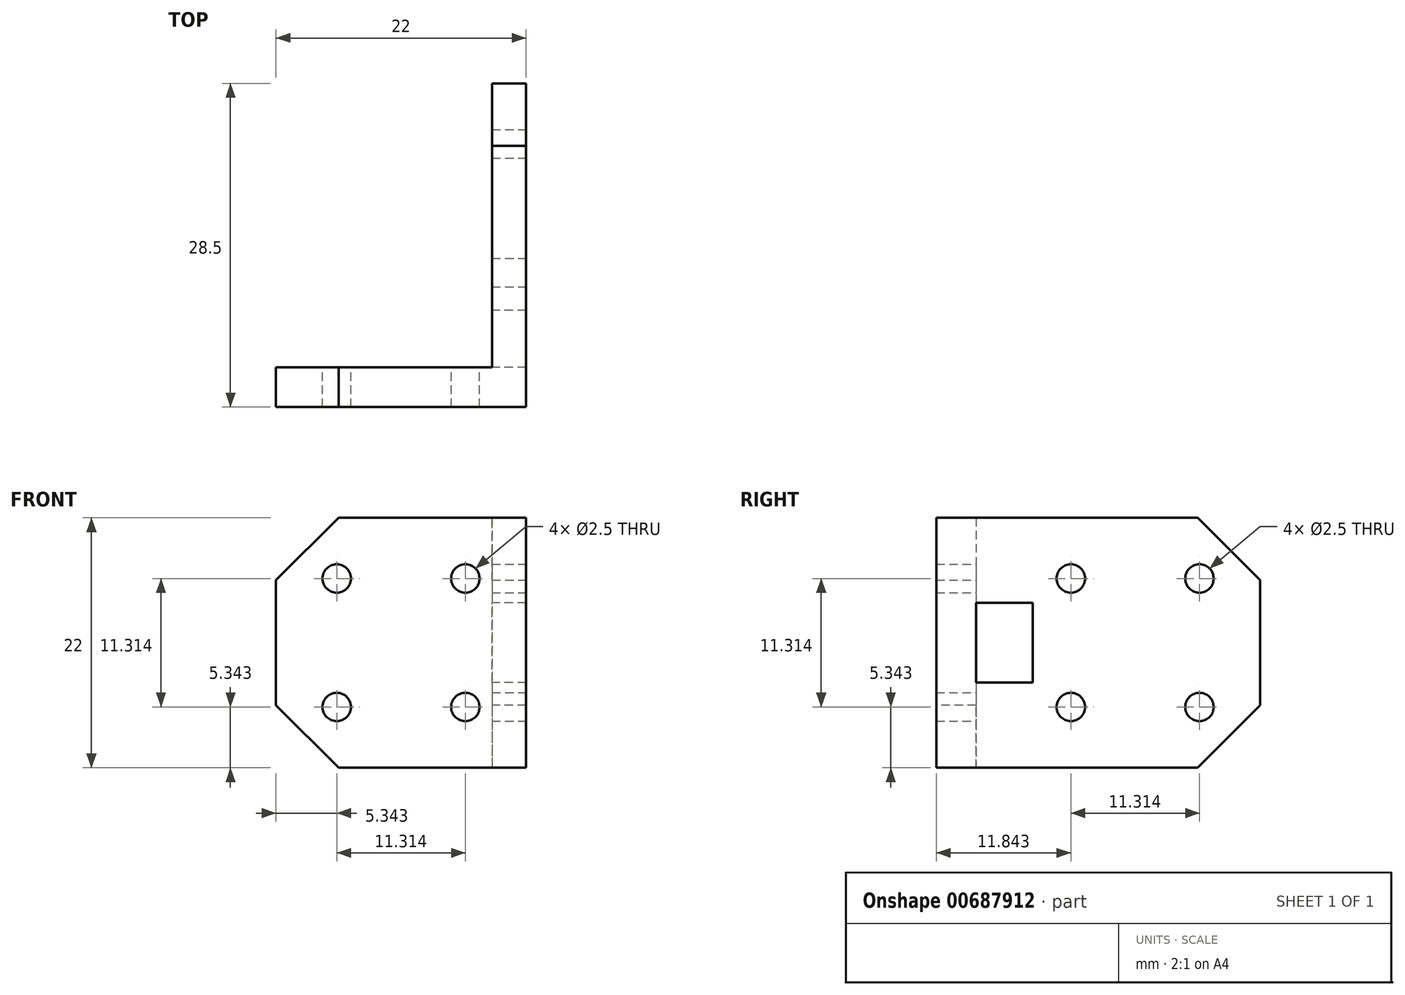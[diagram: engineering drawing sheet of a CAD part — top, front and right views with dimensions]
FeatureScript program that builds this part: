
annotation { "Feature Type Name" : "Feature", "Feature Type Description" : "" }
export const myFeature = defineFeature(function(context is Context, id is Id, definition is map)
    precondition{}
    {
        {
            var Q0;
            Q0=qCreatedBy(makeId("Top.planeOp"),FACE);
            var sketch = newSketch(context, id + "F0", { "sketchPlane" : qUnion([Q0])});
            skLineSegment(sketch, "E0", {"start": v(8, 11) * mm, "end": v(11, 11) * mm});
            skLineSegment(sketch, "E1", {"start": v(11, 11) * mm, "end": v(11, -17.5) * mm});
            skLineSegment(sketch, "E2", {"start": v(11, -17.5) * mm, "end": v(-11, -17.5) * mm});
            skLineSegment(sketch, "E3", {"start": v(-11, -17.5) * mm, "end": v(-11, -14) * mm});
            skLineSegment(sketch, "E4", {"start": v(-11, -14) * mm, "end": v(8, -14) * mm});
            skLineSegment(sketch, "E5", {"start": v(8, -14) * mm, "end": v(8, 11) * mm});
            skSolve(sketch);
        }
        {
            var Q0;
            Q0 = qSketchRegion(id + "F0", true);
            extrude(context, id + "F1", {"entities" : qUnion([Q0]), "endBound" : BoundingType.SYMMETRIC, "depth" : 22 * mm, "offsetDistance" : 25 * mm});
        }
        {
            var Q0;
            Q0=makeQuery(id+"F1.opExtrude","SWEPT_FACE",FACE,{"disambiguationData":[OSD([sQuery(id+"F0.wireOp",EDGE,"E1")])]});
            var sketch = newSketch(context, id + "F2", { "sketchPlane" : qUnion([Q0])});
            skCircle(sketch, "E6", {"center": v(5.66, -5.66) * mm, "radius": 1.25 * mm});
            skLineSegment(sketch, "E7", {"start": v(0, 0) * mm, "end": v(11, -11) * mm, "construction": true});
            skCircle(sketch, "E8.1.0", {"center": v(5.66, 5.66) * mm, "radius": 1.25 * mm});
            skCircle(sketch, "E8.2.0", {"center": v(-5.66, 5.66) * mm, "radius": 1.25 * mm});
            skCircle(sketch, "E8.3.0", {"center": v(-5.66, -5.66) * mm, "radius": 1.25 * mm});
            skPoint(sketch, "E8.center", {"position": v(0, 0) * mm});
            skSolve(sketch);
        }
        {
            var Q0;
            Q0 = qSketchRegion(id + "F2", true);
            extrude(context, id + "F3", {"entities" : qUnion([Q0]), "operationType" : NewBodyOperationType.REMOVE, "endBound" : BoundingType.THROUGH_ALL, "oppositeDirection" : true, "depth" : 25 * mm, "offsetDistance" : 25 * mm});
        }
        {
            var Q0;
            Q0=makeQuery(id+"F1.opExtrude","SWEPT_FACE",FACE,{"disambiguationData":[OSD([sQuery(id+"F0.wireOp",EDGE,"E4")])]});
            var sketch = newSketch(context, id + "F4", { "sketchPlane" : qUnion([Q0])});
            skCircle(sketch, "E9", {"center": v(5.66, -5.66) * mm, "radius": 1.25 * mm});
            skLineSegment(sketch, "E10", {"start": v(11, -11) * mm, "end": v(0, 0) * mm, "construction": true});
            skCircle(sketch, "E11.1.0", {"center": v(5.66, 5.66) * mm, "radius": 1.25 * mm});
            skCircle(sketch, "E11.2.0", {"center": v(-5.66, 5.66) * mm, "radius": 1.25 * mm});
            skCircle(sketch, "E11.3.0", {"center": v(-5.66, -5.66) * mm, "radius": 1.25 * mm});
            skPoint(sketch, "E11.center", {"position": v(0, 0) * mm});
            skSolve(sketch);
        }
        {
            var Q0;
            Q0 = qSketchRegion(id + "F4", true);
            extrude(context, id + "F5", {"entities" : qUnion([Q0]), "operationType" : NewBodyOperationType.REMOVE, "endBound" : BoundingType.THROUGH_ALL, "oppositeDirection" : true, "depth" : 25 * mm, "offsetDistance" : 25 * mm});
        }
        {
            var Q0;
            Q0=makeQuery(id+"F1.opExtrude","CAP_EDGE",EDGE,{"disambiguationData":[OSD([sQuery(id+"F0.wireOp",EDGE,"E0")])],"isStart":false});
            var Q1;
            Q1=makeQuery(id+"F1.opExtrude","CAP_EDGE",EDGE,{"disambiguationData":[OSD([sQuery(id+"F0.wireOp",EDGE,"E0")])],"isStart":true});
            var Q2;
            Q2=makeQuery(id+"F1.opExtrude","CAP_EDGE",EDGE,{"disambiguationData":[OSD([sQuery(id+"F0.wireOp",EDGE,"E3")])],"isStart":true});
            var Q3;
            Q3=makeQuery(id+"F1.opExtrude","CAP_EDGE",EDGE,{"disambiguationData":[OSD([sQuery(id+"F0.wireOp",EDGE,"E3")])],"isStart":false});
            chamfer(context, id + "F6", {"entities" : qUnion([Q0, Q1, Q2, Q3]), "width" : 5.5 * mm, "tangentPropagation" : true});
        }
        {
            var Q0;
            Q0=makeQuery(id+"F1.opExtrude","SWEPT_FACE",FACE,{"disambiguationData":[OSD([sQuery(id+"F0.wireOp",EDGE,"E5")])]});
            var sketch = newSketch(context, id + "F7", { "sketchPlane" : qUnion([Q0])});
            skLineSegment(sketch, "E12.bottom", {"start": v(14, -3.5) * mm, "end": v(9, -3.5) * mm});
            skLineSegment(sketch, "E12.top", {"start": v(14, 3.5) * mm, "end": v(9, 3.5) * mm});
            skLineSegment(sketch, "E12.left", {"start": v(14, -3.5) * mm, "end": v(14, 3.5) * mm});
            skLineSegment(sketch, "E12.right", {"start": v(9, -3.5) * mm, "end": v(9, 3.5) * mm});
            skSolve(sketch);
        }
        {
            var Q0;
            Q0 = qSketchRegion(id + "F7", true);
            extrude(context, id + "F8", {"entities" : qUnion([Q0]), "operationType" : NewBodyOperationType.REMOVE, "oppositeDirection" : true, "depth" : 25 * mm, "offsetDistance" : 25 * mm});
        }
    });
